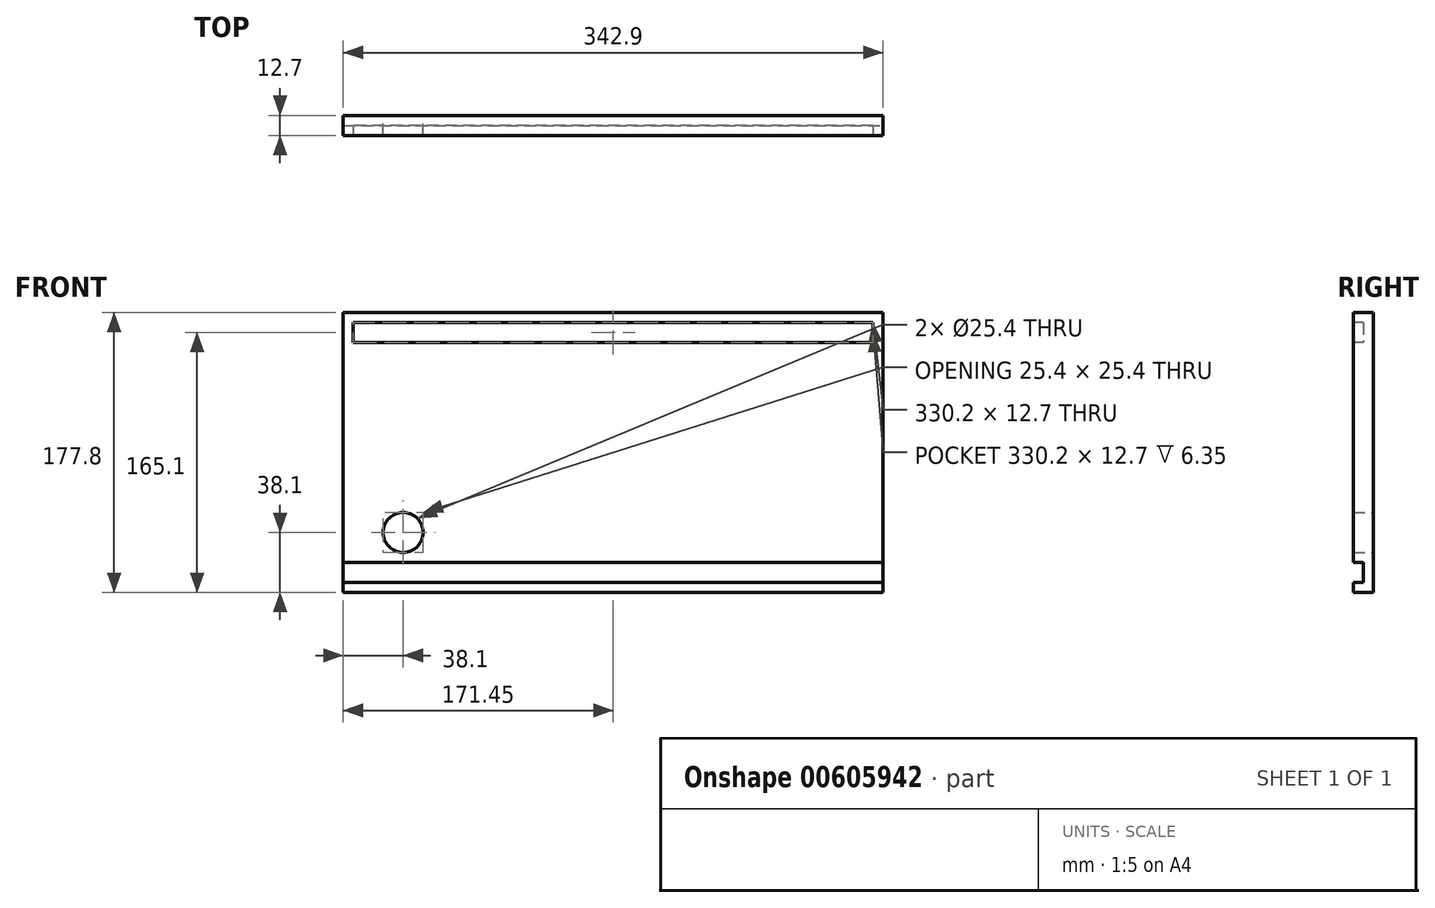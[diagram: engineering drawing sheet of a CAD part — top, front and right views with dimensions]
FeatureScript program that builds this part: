
annotation { "Feature Type Name" : "Feature", "Feature Type Description" : "" }
export const myFeature = defineFeature(function(context is Context, id is Id, definition is map)
    precondition{}
    {
        {
            var Q0;
            Q0=qCreatedBy(makeId("Front.planeOp"),FACE);
            var sketch = newSketch(context, id + "F0", { "sketchPlane" : qUnion([Q0])});
            skLineSegment(sketch, "E0.bottom", {"start": v(0, 0) * mm, "end": v(342.9, 0) * mm});
            skLineSegment(sketch, "E0.top", {"start": v(0, 177.8) * mm, "end": v(342.9, 177.8) * mm});
            skLineSegment(sketch, "E0.left", {"start": v(0, 0) * mm, "end": v(0, 177.8) * mm});
            skLineSegment(sketch, "E0.right", {"start": v(342.9, 0) * mm, "end": v(342.9, 177.8) * mm});
            skSolve(sketch);
        }
        {
            var Q0;
            Q0=makeQuery(id+"F0.imprint","IMPRINT",FACE,{"disambiguationData":[TD([[makeQuery(id+"F0.imprint","IMPRINT",EDGE,{"derivedFrom":sQuery(id+"F0.wireOp",EDGE,"E0.bottom")}),1.0]])]});
            extrude(context, id + "F1", {"entities" : qUnion([Q0]), "depth" : 12.7 * mm, "offsetDistance" : 25.4 * mm});
        }
        {
            var Q0;
            Q0=makeQuery(id+"F1.opExtrude","CAP_FACE",FACE,{"disambiguationData":[OSD([sQuery(id+"F0.wireOp",EDGE,"E0.bottom"),sQuery(id+"F0.wireOp",EDGE,"E0.top"),sQuery(id+"F0.wireOp",EDGE,"E0.left"),sQuery(id+"F0.wireOp",EDGE,"E0.right")])],"isStart":false});
            var sketch = newSketch(context, id + "F2", { "sketchPlane" : qUnion([Q0])});
            skLineSegment(sketch, "E1", {"start": v(0, 0) * mm, "end": v(0, 6.35) * mm});
            skLineSegment(sketch, "E2", {"start": v(0, 6.35) * mm, "end": v(0, 19.05) * mm});
            skLineSegment(sketch, "E3", {"start": v(0, 19.05) * mm, "end": v(342.9, 19.05) * mm});
            skLineSegment(sketch, "E4", {"start": v(342.9, 19.05) * mm, "end": v(342.9, 6.35) * mm});
            skLineSegment(sketch, "E5", {"start": v(342.9, 6.35) * mm, "end": v(0, 6.35) * mm});
            skLineSegment(sketch, "E6", {"start": v(0, 19.05) * mm, "end": v(6.35, 19.05) * mm});
            skLineSegment(sketch, "E7", {"start": v(6.35, 19.05) * mm, "end": v(6.35, 6.35) * mm});
            skLineSegment(sketch, "E8", {"start": v(6.35, 6.35) * mm, "end": v(342.9, 6.35) * mm});
            skLineSegment(sketch, "E9", {"start": v(342.9, 19.05) * mm, "end": v(336.55, 19.05) * mm});
            skLineSegment(sketch, "E10", {"start": v(336.55, 19.05) * mm, "end": v(336.55, 6.35) * mm});
            skSolve(sketch);
        }
        {
            var Q0;
            Q0=makeQuery(id+"F2.imprint","IMPRINT",FACE,{"disambiguationData":[TD([[makeQuery(id+"F2.imprint","IMPRINT",EDGE,{"derivedFrom":sQuery(id+"F2.wireOp",EDGE,"E3")}),-1.0]])]});
            extrude(context, id + "F3", {"entities" : qUnion([Q0]), "operationType" : NewBodyOperationType.REMOVE, "oppositeDirection" : true, "depth" : 6.35 * mm, "offsetDistance" : 25.4 * mm});
        }
        {
            var Q0;
            Q0=makeQuery(id+"F1.opExtrude","CAP_FACE",FACE,{"disambiguationData":[OSD([sQuery(id+"F0.wireOp",EDGE,"E0.bottom"),sQuery(id+"F0.wireOp",EDGE,"E0.top"),sQuery(id+"F0.wireOp",EDGE,"E0.left"),sQuery(id+"F0.wireOp",EDGE,"E0.right")])],"isStart":false});
            var sketch = newSketch(context, id + "F4", { "sketchPlane" : qUnion([Q0])});
            skLineSegment(sketch, "E11", {"start": v(0, 177.8) * mm, "end": v(0, 171.45) * mm});
            skLineSegment(sketch, "E12", {"start": v(0, 171.45) * mm, "end": v(0, 158.75) * mm});
            skLineSegment(sketch, "E13", {"start": v(0, 158.75) * mm, "end": v(342.9, 158.75) * mm});
            skLineSegment(sketch, "E14", {"start": v(342.9, 158.75) * mm, "end": v(342.9, 171.45) * mm});
            skLineSegment(sketch, "E15", {"start": v(342.9, 171.45) * mm, "end": v(0, 171.45) * mm});
            skLineSegment(sketch, "E16", {"start": v(0, 158.75) * mm, "end": v(6.35, 158.75) * mm});
            skLineSegment(sketch, "E17", {"start": v(6.35, 158.75) * mm, "end": v(6.35, 171.45) * mm});
            skLineSegment(sketch, "E18", {"start": v(6.35, 171.45) * mm, "end": v(342.9, 171.45) * mm});
            skLineSegment(sketch, "E19", {"start": v(342.9, 171.45) * mm, "end": v(336.55, 171.45) * mm});
            skLineSegment(sketch, "E20", {"start": v(336.55, 171.45) * mm, "end": v(336.55, 158.75) * mm});
            skSolve(sketch);
        }
        {
            var Q0;
            {var subQ0=sQuery(id+"F4.wireOp",EDGE,"E17");Q0=makeQuery(id+"F4.imprint","IMPRINT",FACE,{"disambiguationData":[TD([[makeQuery(id+"F4.imprint","IMPRINT",EDGE,{"derivedFrom":subQ0}),-1.0]])]});}
            extrude(context, id + "F5", {"entities" : qUnion([Q0]), "operationType" : NewBodyOperationType.REMOVE, "oppositeDirection" : true, "depth" : 6.35 * mm, "offsetDistance" : 25.4 * mm});
        }
        {
            var Q0;
            Q0=makeQuery(id+"F1.opExtrude","CAP_FACE",FACE,{"disambiguationData":[OSD([sQuery(id+"F0.wireOp",EDGE,"E0.bottom"),sQuery(id+"F0.wireOp",EDGE,"E0.top"),sQuery(id+"F0.wireOp",EDGE,"E0.left"),sQuery(id+"F0.wireOp",EDGE,"E0.right")])],"isStart":true});
            var sketch = newSketch(context, id + "F6", { "sketchPlane" : qUnion([Q0])});
            skCircle(sketch, "E21", {"center": v(-38.1, 38.1) * mm, "radius": 12.7 * mm});
            skSolve(sketch);
        }
        {
            var Q0;
            Q0=makeQuery(id+"F6.imprint","IMPRINT",FACE,{"disambiguationData":[TD([[makeQuery(id+"F6.imprint","IMPRINT",EDGE,{"derivedFrom":sQuery(id+"F6.wireOp",EDGE,"E21")}),1.0]])]});
            extrude(context, id + "F7", {"entities" : qUnion([Q0]), "operationType" : NewBodyOperationType.REMOVE, "oppositeDirection" : true, "depth" : 25.4 * mm, "offsetDistance" : 25.4 * mm});
        }
    });
